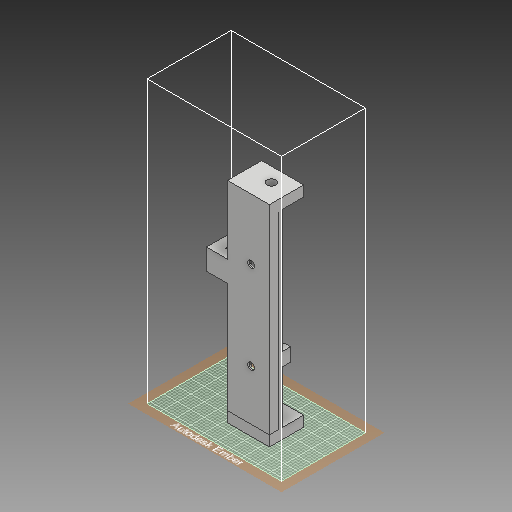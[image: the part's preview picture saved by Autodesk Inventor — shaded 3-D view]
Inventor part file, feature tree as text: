
AUTODESK INVENTOR PART (.ipt)
format: ipt  version: 2018 (Build 220112000, 112)  size: 744,448 bytes
history: native  units: mm
features: sketch x60, extrude x43, hole x8, fillet x6
ambient origin geometry x8: Origin, YZ Plane, XZ Plane, XY Plane, X Axis, Y Axis, Z Axis, Center Point
bodies: Solid1 (feature_tree)
feature tree (117):
  extrude  "Extrusion1"  Depth=100.0mm
  extrude  "Extrusion2"  Depth=5.0mm
  sketch  "Sketch3"  dims[d5=5.0mm d6=40.0mm d7=0.0mm]
  hole  "Hole1"  [1 undecoded]
  extrude  "Extrusion3"  Depth=2.0mm
  hole  "Hole2"  [1 undecoded]
  fillet  "Fillet1"  Radius=8.5mm
  extrude  "Extrusion4"  TaperAngle=90.0deg  [1 undecoded]
  extrude  "Extrusion5"  TaperAngle=180.0deg  [1 undecoded]
  hole  "Hole3"  [1 undecoded]
  fillet  "Fillet2"  Radius=3.5mm
  extrude  "Extrusion6"  Depth=10.0mm
  extrude  "Extrusion7"  Depth=5.0mm TaperAngle=0.0deg
  extrude  "Extrusion8"  Depth=5.0mm TaperAngle=0.0deg
  extrude  "Extrusion9"  Depth=0.1mm
  hole  "Hole4"  [1 undecoded]
  extrude  "Extrusion10"  Depth=5.5mm
  hole  "Hole5"  [1 undecoded]
  extrude  "Extrusion11"  Depth=2.1mm TaperAngle=0.0deg
  extrude  "Extrusion12"  Depth=5.0mm
  extrude  "Extrusion13"  Depth=1.0mm TaperAngle=0.0deg
  extrude  "Extrusion14"  Depth=3.8mm TaperAngle=0.0deg
  sketch  "Sketch21"  dims[d66=6.35mm d67=3.8mm d68=0.0mm]
  extrude  "Extrusion15"  Depth=8.0mm TaperAngle=0.0deg
  sketch  "Sketch23"  dims[d78=3.3mm d79=6.0mm d80=4.0mm d81=2.0mm d82=90.0deg d83=80.0mm d84=20.594885mm d85=5.45mm]
  extrude  "Extrusion16"  Depth=2.0mm
  extrude  "Extrusion17"  Depth=10.5mm
  hole  "Hole6"  [1 undecoded]
  fillet  "Fillet3"  Radius=4.5mm
  extrude  "Extrusion18"  Depth=8.0mm TaperAngle=0.0deg
  sketch  "Sketch28"  dims[d100=4.1mm d101=0.0mm d102=5.0mm]
  extrude  "Extrusion19"  Depth=10.0mm
  extrude  "Extrusion20"  Depth=5.0mm
  extrude  "Extrusion21"  Depth=10.0mm TaperAngle=0.0deg
  hole  "Hole7"  [1 undecoded]
  extrude  "Extrusion22"  Depth=21.0mm
  extrude  "Extrusion23"  Depth=118.0mm TaperAngle=0.0deg
  fillet  "Fillet4"  Radius=50.0mm
  fillet  "Fillet5"  Radius=7.499983mm
  extrude  "Extrusion24"  Depth=10.0mm
  extrude  "Extrusion25"  Depth=4.1mm TaperAngle=0.0deg
  hole  "Hole8"  [1 undecoded]
  extrude  "Extrusion26"  Depth=8.0mm TaperAngle=0.0deg
  sketch  "Sketch39"  dims[d142=3.85mm d143=0.0mm d144=3.0mm]
  extrude  "Extrusion27"  Depth=1.0mm
  extrude  "Extrusion28"  Depth=3.0mm
  extrude  "Extrusion29"  Depth=100.0mm TaperAngle=0.0deg
  extrude  "Extrusion30"  Depth=10.0mm
  extrude  "Extrusion31"  Depth=5.0mm
  fillet  "Fillet6"  Radius=7.5mm
  extrude  "Extrusion32"  Depth=8.0mm
  sketch  "Sketch46"  dims[d167=2.0mm d168=0.0mm d169=2.0mm d170=0.0mm]
  extrude  "Extrusion33"  Depth=5.0mm TaperAngle=0.0deg
  sketch  "Sketch48"  dims[d174=3.3mm d175=10.0mm d176=0.0mm]
  extrude  "Extrusion34"  Depth=2.0mm TaperAngle=0.0deg
  extrude  "Extrusion35"  Depth=2.0mm
  sketch  "Sketch51"  dims[d182=5.0mm d183=9.5mm d184=0.0mm]
  extrude  "Extrusion36"  Depth=10.0mm TaperAngle=0.0deg
  sketch  "Sketch53"  dims[d189=5.0mm d190=3.5mm]
  extrude  "Extrusion37"  Depth=3.5mm
  sketch  "Sketch55"  dims[d194=8.5mm d195=12.0mm]
  extrude  "Extrusion38"  Depth=8.5mm
  extrude  "Extrusion39"  Depth=9.5mm TaperAngle=0.0deg
  extrude  "Extrusion40"  Depth=9.5mm TaperAngle=0.0deg
  extrude  "Extrusion41"  Depth=3.5mm
  extrude  "Extrusion42"  Depth=9.5mm TaperAngle=0.0deg
  extrude  "Extrusion43"  Depth=12.0mm
  sketch  "Sketch1"  dims[d0=22.65mm d1=100.0mm]
  sketch  "Sketch2"  dims[d2=5.0mm d3=0.0mm d4=5.0mm]
  sketch  "Sketch4"  dims[d8=10.0mm]
  sketch  "Sketch5"  dims[d9=4.0mm d10=6.0mm d11=4.0mm d12=2.0mm d13=90.0deg d14=115.0mm d15=20.594885mm d16=23.0mm]
  sketch  "Sketch6"  dims[d17=102.75mm d18=0.0mm d19=1.175mm d20=8.5mm]
  sketch  "Sketch7"  dims[d21=21.0mm d22=90.0deg]
  sketch  "Sketch8"  dims[d23=8.5mm d24=180.0deg]
  sketch  "Sketch9"  dims[d25=21.0mm]
  sketch  "Sketch10"  dims[d26=4.0mm d27=6.0mm d28=4.0mm d29=2.0mm d30=90.0deg d31=115.0mm d32=20.594885mm d33=1.0mm d34=3.5mm]
  sketch  "Sketch11"  dims[d35=15.825mm d36=10.0mm]
  sketch  "Sketch12"  dims[d37=10.0mm d38=5.0mm d39=0.0mm]
  sketch  "Sketch13"  dims[d40=5.0mm d41=12.5mm d42=0.0mm]
  sketch  "Sketch14"  dims[d43=6.0mm d44=6.0mm d45=4.0mm d46=2.0mm d47=90.0deg d48=115.0mm d49=20.594885mm d50=0.1mm]
  sketch  "Sketch15"  dims[d51=4.25mm d52=1000.0mm d53=0.0mm]
  sketch  "Sketch16"  dims[d54=3.3mm d55=5.5mm]
  sketch  "Sketch17"  dims[d56=3.2mm d57=3.0mm]
  sketch  "Sketch18"  dims[d58=2.1mm d59=91.25mm d60=0.0mm]
  sketch  "Sketch19"  dims[d61=4.44mm d62=5.0mm]
  sketch  "Sketch20"  dims[d63=1.0mm d64=91.25mm d65=0.0mm]
  sketch  "Sketch22"  dims[d69=3.3mm d70=6.0mm d71=4.0mm d72=2.0mm d73=90.0deg d74=8.0mm d75=20.594885mm d76=4.55mm d77=0.0mm]
  sketch  "Sketch24"  dims[d86=129.8mm d87=0.0mm d88=10.5mm]
  sketch  "Sketch25"  dims[d89=2.5mm d90=0.0mm d91=10.0mm d92=4.5mm d93=0.0mm]
  sketch  "Sketch26"  dims[d94=8.0mm d95=0.0mm d96=15.5mm d97=0.0mm]
  sketch  "Sketch27"  dims[d98=10.0mm d99=10.0mm]
  sketch  "Sketch29"  dims[d103=17.5mm d104=10.0mm d105=0.0mm]
  sketch  "Sketch30"  dims[d106=5.0mm]
  sketch  "Sketch31"  dims[d107=6.0mm d108=6.0mm d109=4.0mm d110=2.0mm d111=90.0deg d112=80.0mm d113=20.594885mm d114=2.0mm]
  sketch  "Sketch32"  dims[d115=45.0mm d116=0.0mm d117=21.0mm]
  sketch  "Sketch33"  dims[d118=4.5mm d119=118.0mm d120=0.0mm d121=50.0mm d122=7.499983mm]
  sketch  "Sketch34"  dims[d123=7.5mm d124=10.0mm]
  sketch  "Sketch35"  dims[d125=10.0mm d126=4.1mm d127=0.0mm]
  sketch  "Sketch36"  dims[d128=13.4mm d129=0.0mm d130=5.0mm]
  sketch  "Sketch37"  dims[d131=6.0mm d132=6.0mm d133=4.0mm d134=2.0mm d135=90.0deg d136=8.0mm d137=20.594885mm d138=130.4mm d139=0.0mm]
  sketch  "Sketch38"  dims[d140=1.0mm d141=1.0mm]
  sketch  "Sketch40"  dims[d145=2.0mm d146=100.0mm d147=0.0mm]
  sketch  "Sketch41"  dims[d148=4.0mm d149=10.0mm]
  sketch  "Sketch42"  dims[d150=5.0mm d151=15.0mm d152=7.5mm]
  sketch  "Sketch43"  dims[d153=7.5mm d154=0.0mm]
  sketch  "Sketch44"  dims[d155=6.0mm d156=6.0mm d157=4.0mm d158=2.0mm d159=90.0deg d160=8.0mm d161=20.594885mm d162=5.5mm]
  sketch  "Sketch45"  dims[d163=5.0mm d164=0.0mm d165=5.5mm d166=0.0mm]
  sketch  "Sketch47"  dims[d171=2.0mm d172=0.0mm d173=20.0mm]
  sketch  "Sketch49"  dims[d177=2.0mm d178=3.5mm]
  sketch  "Sketch50"  dims[d179=5.0mm d180=0.0mm d181=8.5mm]
  sketch  "Sketch52"  dims[d185=9.5mm d186=0.0mm d187=2.7mm d188=0.0mm]
  sketch  "Sketch54"  dims[d191=7.5mm d192=9.5mm d193=0.0mm]
  sketch  "Sketch56"  dims[d196=10.25mm d197=0.0mm]
  sketch  "Sketch57"  dims[d198=12.0mm]
  sketch  "Sketch58"  dims[d199=10.25mm d200=0.0mm]
  sketch  "Sketch59"  dims[d201=3.5mm d202=0.0mm]
  sketch  "Sketch60"  dims[d203=3.75mm d204=3.5mm d205=0.0mm d206=9.6mm d207=3.2mm d208=0.0mm d209=9.6mm d210=3.2mm d211=0.0mm d212=5.5mm d213=101.0mm d214=0.0mm]
note: 10 required parameter values undecoded (feature->parameter linkage not recoverable at this tier; creation-order binding heuristic only, values carry confidence <= 0.55)
